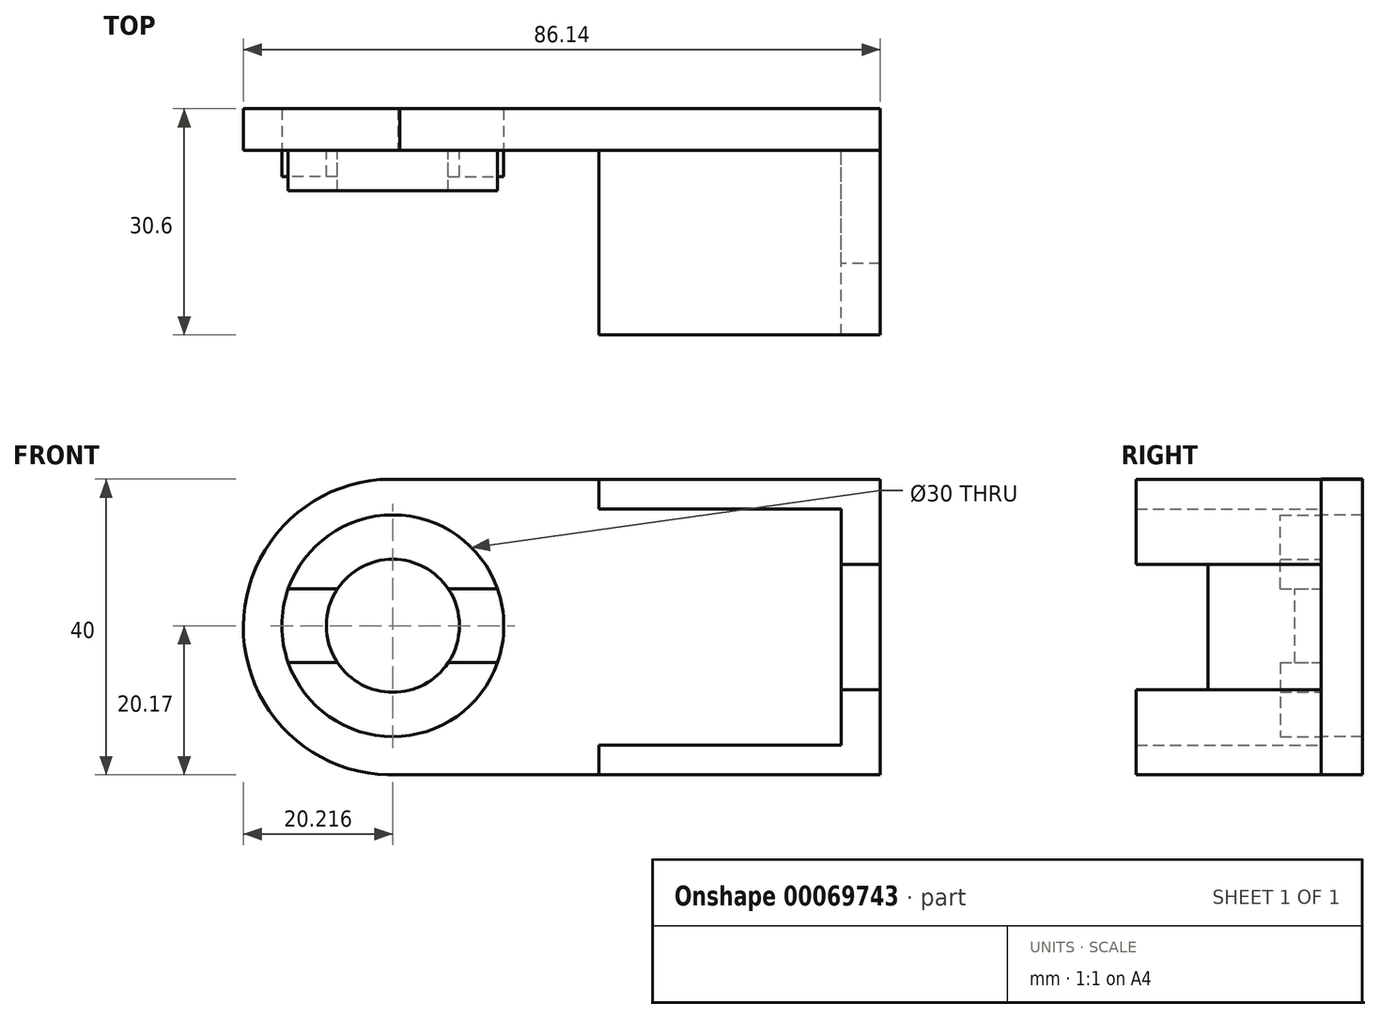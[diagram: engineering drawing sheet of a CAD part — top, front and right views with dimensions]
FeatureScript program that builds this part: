
annotation { "Feature Type Name" : "Feature", "Feature Type Description" : "" }
export const myFeature = defineFeature(function(context is Context, id is Id, definition is map)
    precondition{}
    {
        {
            var Q0;
            Q0=qCreatedBy(makeId("Front.planeOp"),FACE);
            var sketch = newSketch(context, id + "F0", { "sketchPlane" : qUnion([Q0])});
            skCircle(sketch, "E0", {"center": v(-51.7, 0) * mm, "radius": 9 * mm});
            skCircle(sketch, "E1", {"center": v(-51.7, 0) * mm, "radius": 15 * mm});
            skLineSegment(sketch, "E2", {"start": v(-59.18, 5) * mm, "end": v(-65.84, 5) * mm});
            skLineSegment(sketch, "E3", {"start": v(-59.18, -5) * mm, "end": v(-65.84, -5) * mm});
            skLineSegment(sketch, "E4", {"start": v(-44.21, 5) * mm, "end": v(-37.55, 5) * mm});
            skLineSegment(sketch, "E5", {"start": v(-44.21, -5) * mm, "end": v(-37.55, -5) * mm});
            skArc(sketch, "E6", {"start": v(-50.77, 19.8) * mm, "mid": v(-71.91, -0.05) * mm, "end": v(-51.01, -20.15) * mm});
            skLineSegment(sketch, "E7", {"start": v(-50.77, 19.8) * mm, "end": v(-10.77, 19.8) * mm});
            skLineSegment(sketch, "E8", {"start": v(-51.01, -20.15) * mm, "end": v(-10.77, -20.15) * mm});
            skLineSegment(sketch, "E9", {"start": v(-10.77, 19.8) * mm, "end": v(14.23, 19.8) * mm});
            skLineSegment(sketch, "E10", {"start": v(-10.77, -20.15) * mm, "end": v(14.23, -20.15) * mm});
            skLineSegment(sketch, "E11", {"start": v(-10.77, 19.8) * mm, "end": v(-10.77, 15.8) * mm});
            skLineSegment(sketch, "E12", {"start": v(-10.77, 15.8) * mm, "end": v(-23.83, 15.8) * mm});
            skLineSegment(sketch, "E13", {"start": v(-23.83, 15.8) * mm, "end": v(-23.83, 19.8) * mm});
            skLineSegment(sketch, "E14", {"start": v(-10.77, -20.15) * mm, "end": v(-10.77, -16.15) * mm});
            skLineSegment(sketch, "E15", {"start": v(-10.77, -16.15) * mm, "end": v(-23.83, -16.15) * mm});
            skLineSegment(sketch, "E16", {"start": v(-23.83, -16.15) * mm, "end": v(-23.83, -20.15) * mm});
            skLineSegment(sketch, "E17", {"start": v(14.23, 19.8) * mm, "end": v(14.23, 8.3) * mm});
            skLineSegment(sketch, "E18", {"start": v(14.23, -20.15) * mm, "end": v(14.23, -8.65) * mm});
            skLineSegment(sketch, "E19", {"start": v(8.9, 8.3) * mm, "end": v(8.9, 15.8) * mm});
            skLineSegment(sketch, "E20", {"start": v(8.9, 15.8) * mm, "end": v(-10.77, 15.8) * mm});
            skLineSegment(sketch, "E21", {"start": v(8.9, -8.65) * mm, "end": v(8.9, -16.15) * mm});
            skLineSegment(sketch, "E22", {"start": v(8.9, -16.15) * mm, "end": v(-10.77, -16.15) * mm});
            skLineSegment(sketch, "E23", {"start": v(14.23, 8.3) * mm, "end": v(3.58, 8.3) * mm});
            skLineSegment(sketch, "E24", {"start": v(14.23, -8.65) * mm, "end": v(3.58, -8.65) * mm});
            skLineSegment(sketch, "E25", {"start": v(8.9, 8.3) * mm, "end": v(8.9, -8.65) * mm});
            skLineSegment(sketch, "E26", {"start": v(14.23, -8.65) * mm, "end": v(14.23, 8.3) * mm});
            skSolve(sketch);
        }
        {
            var Q0;
            {var subQ0=sQuery(id+"F0.wireOp",EDGE,"E11");Q0=makeQuery(id+"F0.imprint","IMPRINT",FACE,{"disambiguationData":[TD([[makeQuery(id+"F0.imprint","IMPRINT",EDGE,{"derivedFrom":subQ0}),-1.0]])]});}
            var Q1;
            {var subQ0=sQuery(id+"F0.wireOp",EDGE,"E14");Q1=makeQuery(id+"F0.imprint","IMPRINT",FACE,{"disambiguationData":[TD([[makeQuery(id+"F0.imprint","IMPRINT",EDGE,{"derivedFrom":subQ0}),1.0]])]});}
            var Q2;
            Q2=makeQuery(id+"F0.imprint","IMPRINT",FACE,{"disambiguationData":[TD([[makeQuery(id+"F0.imprint","IMPRINT",EDGE,{"derivedFrom":sQuery(id+"F0.wireOp",EDGE,"E9")}),-1.0]])]});
            var Q3;
            Q3=makeQuery(id+"F0.imprint","IMPRINT",FACE,{"disambiguationData":[TD([[makeQuery(id+"F0.imprint","IMPRINT",EDGE,{"derivedFrom":sQuery(id+"F0.wireOp",EDGE,"E10")}),1.0]])]});
            extrude(context, id + "F1", {"entities" : qUnion([Q0, Q1, Q2, Q3]), "depth" : 25 * mm});
        }
        {
            var Q0;
            {var subQ2=sQuery(id+"F0.wireOp",EDGE,"E25");Q0=makeQuery(id+"F0.imprint","IMPRINT",FACE,{"disambiguationData":[TD([[makeQuery(id+"F0.imprint","IMPRINT",EDGE,{"derivedFrom":subQ2}),1.0]])]});}
            extrude(context, id + "F2", {"entities" : qUnion([Q0]), "depth" : 15.3 * mm});
        }
        {
            var Q0;
            Q0 = qSketchRegion(id + "F0", true);
            var Q1;
            {var subQ6=sQuery(id+"F0.wireOp",EDGE,"E6");Q1=makeQuery(id+"F0.imprint","IMPRINT",FACE,{"disambiguationData":[TD([[makeQuery(id+"F0.imprint","IMPRINT",EDGE,{"derivedFrom":subQ6}),1.0]])]});}
            extrude(context, id + "F3", {"entities" : qUnion([Q0, Q1]), "oppositeDirection" : true, "depth" : 5.6 * mm});
        }
        {
            var Q0;
            {var subQ0=sQuery(id+"F0.wireOp",EDGE,"E3");Q0=makeQuery(id+"F0.imprint","IMPRINT",FACE,{"disambiguationData":[TD([[makeQuery(id+"F0.imprint","IMPRINT",EDGE,{"derivedFrom":subQ0}),1.0]])]});}
            var Q1;
            {var subQ0=sQuery(id+"F0.wireOp",EDGE,"E2");Q1=makeQuery(id+"F0.imprint","IMPRINT",FACE,{"disambiguationData":[TD([[makeQuery(id+"F0.imprint","IMPRINT",EDGE,{"derivedFrom":subQ0}),-1.0]])]});}
            extrude(context, id + "F4", {"entities" : qUnion([Q0, Q1]), "depth" : 5.5 * mm});
        }
        {
            var Q0;
            {var subQ0=sQuery(id+"F0.wireOp",EDGE,"E2");Q0=makeQuery(id+"F0.imprint","IMPRINT",FACE,{"disambiguationData":[TD([[makeQuery(id+"F0.imprint","IMPRINT",EDGE,{"derivedFrom":subQ0}),1.0]])]});}
            var Q1;
            {var subQ0=sQuery(id+"F0.wireOp",EDGE,"E4");Q1=makeQuery(id+"F0.imprint","IMPRINT",FACE,{"disambiguationData":[TD([[makeQuery(id+"F0.imprint","IMPRINT",EDGE,{"derivedFrom":subQ0}),-1.0]])]});}
            extrude(context, id + "F5", {"entities" : qUnion([Q0, Q1]), "depth" : 3.55 * mm});
        }
    });
